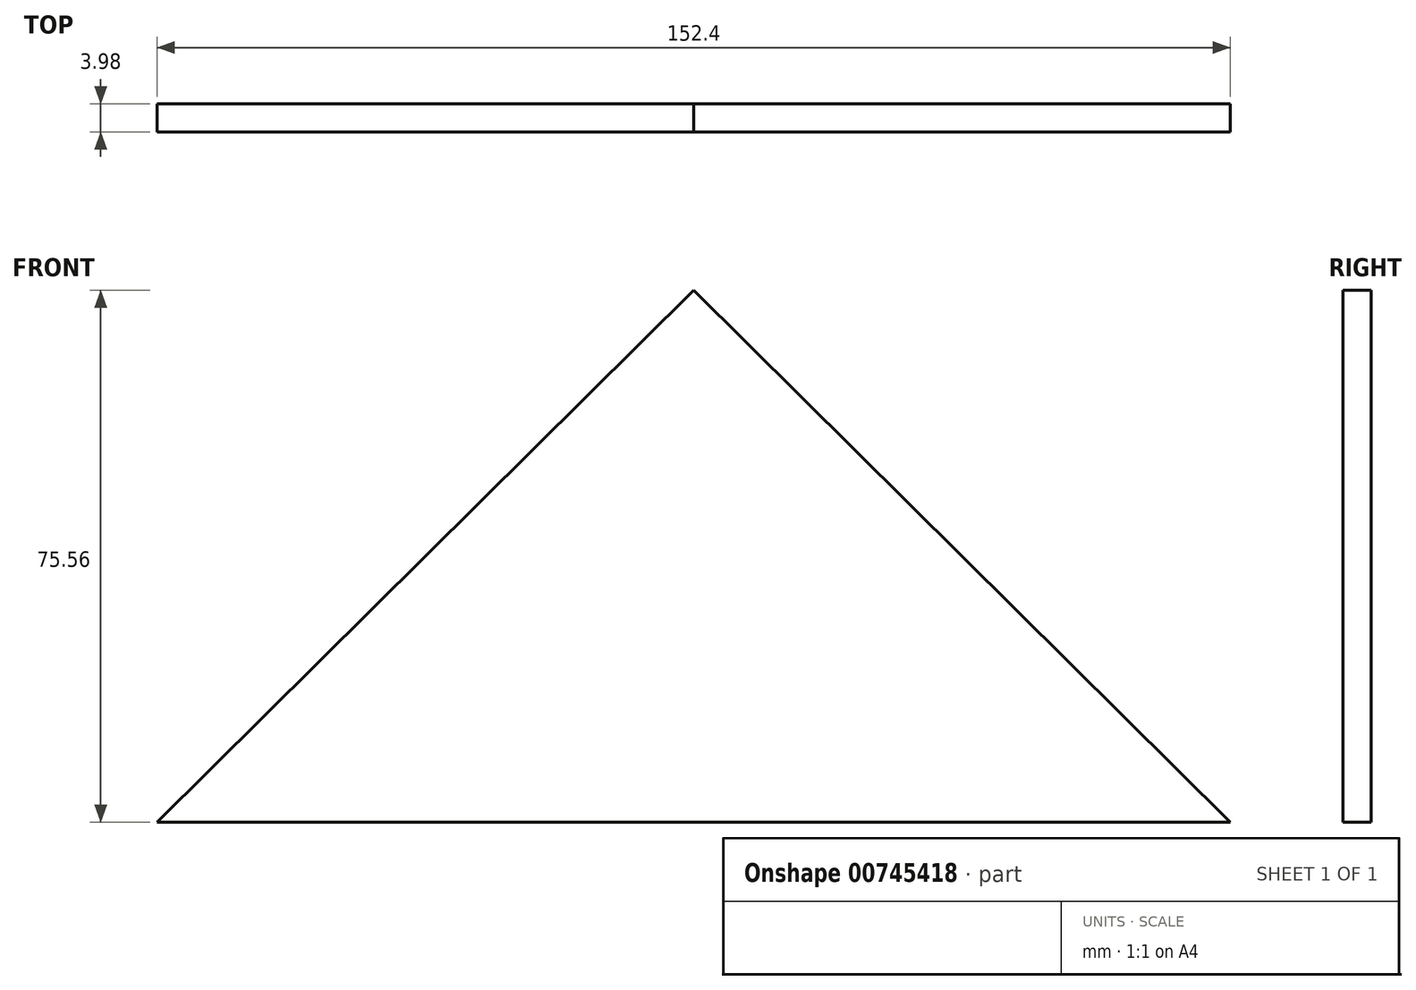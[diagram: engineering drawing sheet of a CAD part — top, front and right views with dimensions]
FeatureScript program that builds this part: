
annotation { "Feature Type Name" : "Feature", "Feature Type Description" : "" }
export const myFeature = defineFeature(function(context is Context, id is Id, definition is map)
    precondition{}
    {
        {
            var Q0;
            Q0=qCreatedBy(makeId("Front.planeOp"),FACE);
            var sketch = newSketch(context, id + "F0", { "sketchPlane" : qUnion([Q0])});
            skLineSegment(sketch, "E0", {"start": v(0, 0) * mm, "end": v(-76.2, 0) * mm});
            skLineSegment(sketch, "E1", {"start": v(0, 0) * mm, "end": v(76.2, 0) * mm});
            skLineSegment(sketch, "E2", {"start": v(-76.2, 0) * mm, "end": v(0, 75.56) * mm});
            skLineSegment(sketch, "E3", {"start": v(0, 75.56) * mm, "end": v(76.2, 0) * mm});
            skSolve(sketch);
        }
        {
            var Q0;
            Q0=sQuery(id+"F0.wireOp",EDGE,"E0");
            var Q1;
            Q1=sQuery(id+"F0.wireOp",EDGE,"E2");
            var Q2;
            Q2=sQuery(id+"F0.wireOp",EDGE,"E3");
            var Q3;
            Q3=sQuery(id+"F0.wireOp",EDGE,"E1");
            extrude(context, id + "F1", {"bodyType" : ToolBodyType.SURFACE, "surfaceEntities" : qUnion([Q0, Q1, Q2, Q3]), "depth" : 3.98 * mm, "offsetDistance" : 25.4 * mm});
        }
    });
